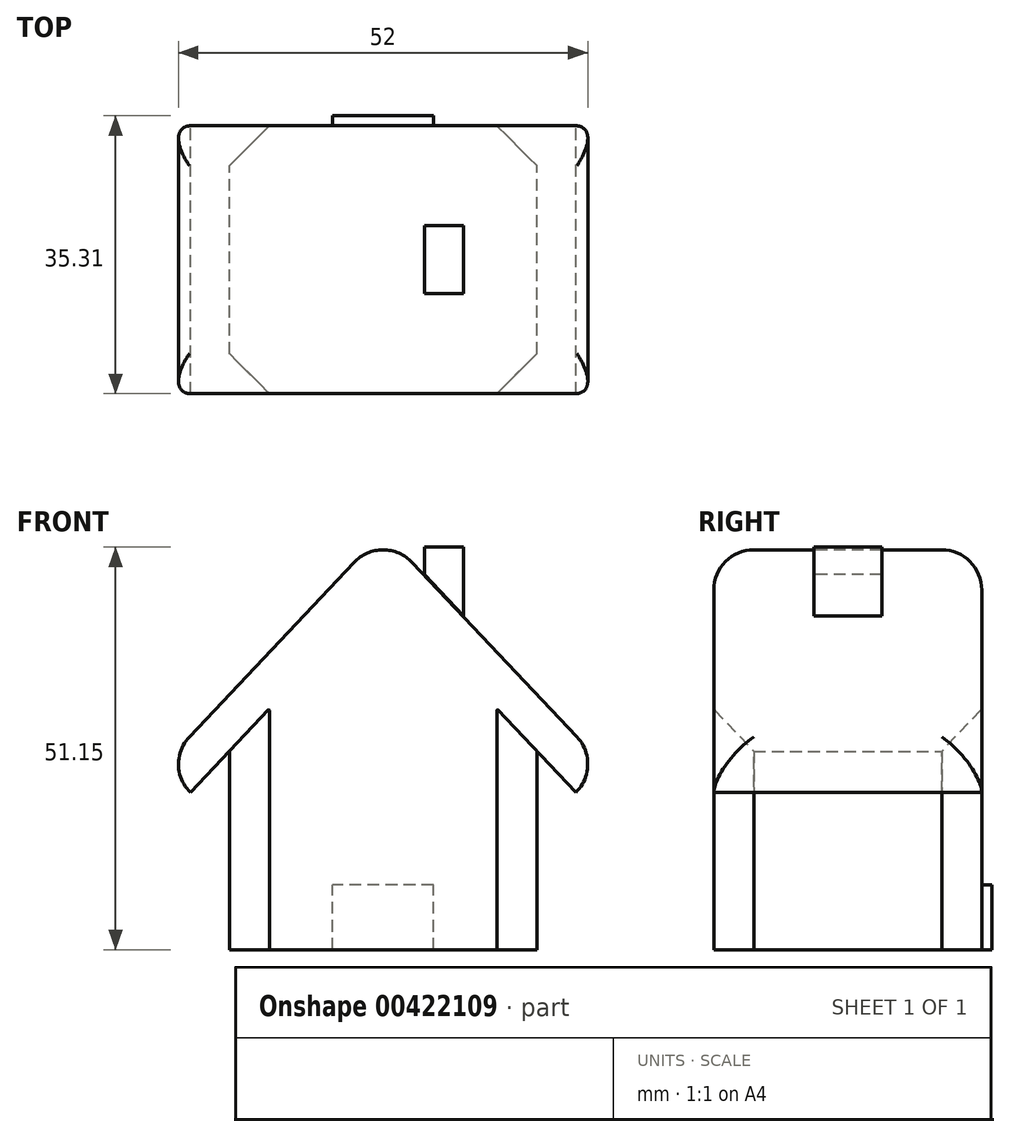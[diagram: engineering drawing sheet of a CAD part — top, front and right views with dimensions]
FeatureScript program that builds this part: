
annotation { "Feature Type Name" : "Feature", "Feature Type Description" : "" }
export const myFeature = defineFeature(function(context is Context, id is Id, definition is map)
    precondition{}
    {
        {
            var Q0;
            Q0=qCreatedBy(makeId("Front.planeOp"),FACE);
            var sketch = newSketch(context, id + "F0", { "sketchPlane" : qUnion([Q0])});
            skLineSegment(sketch, "E0", {"start": v(-19.53, 0) * mm, "end": v(-19.53, 25.21) * mm});
            skLineSegment(sketch, "E1", {"start": v(-19.53, 25.21) * mm, "end": v(-24.48, 19.97) * mm});
            skLineSegment(sketch, "E2", {"start": v(-24.48, 19.97) * mm, "end": v(-28.1, 23.38) * mm});
            skLineSegment(sketch, "E3", {"start": v(-28.1, 23.38) * mm, "end": v(0, 53.13) * mm});
            skLineSegment(sketch, "E4", {"start": v(-19.53, 0) * mm, "end": v(0, 0) * mm});
            skLineSegment(sketch, "E5.MirrorCS", {"start": v(28.1, 23.38) * mm, "end": v(0, 53.13) * mm});
            skLineSegment(sketch, "E6.MirrorCS", {"start": v(24.48, 19.97) * mm, "end": v(28.1, 23.38) * mm});
            skLineSegment(sketch, "E7.MirrorCS", {"start": v(19.53, 25.21) * mm, "end": v(24.48, 19.97) * mm});
            skLineSegment(sketch, "E8.MirrorCS", {"start": v(19.53, 0) * mm, "end": v(19.53, 25.21) * mm});
            skLineSegment(sketch, "E9.MirrorCS", {"start": v(19.53, 0) * mm, "end": v(0, 0) * mm});
            skSolve(sketch);
        }
        {
            var Q0;
            Q0=makeQuery(id+"F0.imprint","IMPRINT",FACE,{"disambiguationData":[TD([[makeQuery(id+"F0.imprint","IMPRINT",EDGE,{"derivedFrom":sQuery(id+"F0.wireOp",EDGE,"E0")}),-1.0]])]});
            extrude(context, id + "F1", {"entities" : qUnion([Q0]), "endBound" : BoundingType.SYMMETRIC, "depth" : 34.04 * mm});
        }
        {
            var Q0;
            Q0=makeQuery(id+"F1.opExtrude","CAP_FACE",FACE,{"disambiguationData":[OSD([sQuery(id+"F0.wireOp",EDGE,"E0"),sQuery(id+"F0.wireOp",EDGE,"E1"),sQuery(id+"F0.wireOp",EDGE,"E2"),sQuery(id+"F0.wireOp",EDGE,"E3"),sQuery(id+"F0.wireOp",EDGE,"E4"),sQuery(id+"F0.wireOp",EDGE,"E5.MirrorCS"),sQuery(id+"F0.wireOp",EDGE,"E6.MirrorCS"),sQuery(id+"F0.wireOp",EDGE,"E7.MirrorCS"),sQuery(id+"F0.wireOp",EDGE,"E8.MirrorCS"),sQuery(id+"F0.wireOp",EDGE,"E9.MirrorCS")])],"isStart":true});
            var sketch = newSketch(context, id + "F2", { "sketchPlane" : qUnion([Q0])});
            skLineSegment(sketch, "E10", {"start": v(-6.4, 0) * mm, "end": v(-6.4, 8.26) * mm});
            skLineSegment(sketch, "E11", {"start": v(0, 8.26) * mm, "end": v(-6.4, 8.26) * mm});
            skLineSegment(sketch, "E12", {"start": v(0, 8.26) * mm, "end": v(0, 0) * mm});
            skLineSegment(sketch, "E13", {"start": v(0, 0) * mm, "end": v(-6.4, 0) * mm});
            skLineSegment(sketch, "E14.MirrorCS", {"start": v(0, 8.26) * mm, "end": v(6.4, 8.26) * mm});
            skLineSegment(sketch, "E15.MirrorCS", {"start": v(6.4, 0) * mm, "end": v(6.4, 8.26) * mm});
            skLineSegment(sketch, "E16.MirrorCS", {"start": v(0, 0) * mm, "end": v(6.4, 0) * mm});
            skSolve(sketch);
        }
        {
            var Q0;
            Q0=makeQuery(id+"F2.imprint","IMPRINT",FACE,{"disambiguationData":[TD([[makeQuery(id+"F2.imprint","IMPRINT",EDGE,{"derivedFrom":sQuery(id+"F2.wireOp",EDGE,"E12")}),1.0]])]});
            var Q1;
            Q1=makeQuery(id+"F2.imprint","IMPRINT",FACE,{"disambiguationData":[TD([[makeQuery(id+"F2.imprint","IMPRINT",EDGE,{"derivedFrom":sQuery(id+"F2.wireOp",EDGE,"E10")}),-1.0]])]});
            extrude(context, id + "F3", {"entities" : qUnion([Q0, Q1]), "operationType" : NewBodyOperationType.ADD, "depth" : 1.27 * mm});
        }
        {
            var Q0;
            Q0=qCreatedBy(makeId("Front.planeOp"),FACE);
            var sketch = newSketch(context, id + "F4", { "sketchPlane" : qUnion([Q0])});
            skLineSegment(sketch, "E17", {"start": v(10.2, 42.4) * mm, "end": v(10.2, 51.15) * mm});
            skLineSegment(sketch, "E18", {"start": v(10.2, 51.15) * mm, "end": v(5.25, 51.15) * mm});
            skLineSegment(sketch, "E19", {"start": v(5.25, 47.66) * mm, "end": v(5.25, 51.15) * mm});
            skLineSegment(sketch, "E20", {"start": v(10.2, 42.4) * mm, "end": v(5.25, 47.66) * mm});
            skSolve(sketch);
        }
        {
            var Q0;
            Q0 = qSketchRegion(id + "F4", true);
            extrude(context, id + "F5", {"entities" : qUnion([Q0]), "endBound" : BoundingType.SYMMETRIC, "oppositeDirection" : true, "depth" : 8.64 * mm});
        }
        {
            var Q0;
            Q0=makeQuery(id+"F1.opExtrude","SWEPT_FACE",FACE,{"disambiguationData":[OSD([sQuery(id+"F0.wireOp",EDGE,"E5.MirrorCS")])]});
            var Q1;
            Q1=makeQuery(id+"F1.opExtrude","SWEPT_FACE",FACE,{"disambiguationData":[OSD([sQuery(id+"F0.wireOp",EDGE,"E3")])]});
            fillet(context, id + "F6", {"entities" : qUnion([Q0, Q1]), "radius" : 5.08 * mm, "tangentPropagation" : true, "allowEdgeOverflow" : false});
        }
        {
            var Q0;
            Q0=makeQuery(id+"F1.opExtrude","CAP_EDGE",EDGE,{"disambiguationData":[OSD([sQuery(id+"F0.wireOp",EDGE,"E8.MirrorCS")])],"isStart":true});
            var Q1;
            Q1=makeQuery(id+"F1.opExtrude","CAP_EDGE",EDGE,{"disambiguationData":[OSD([sQuery(id+"F0.wireOp",EDGE,"E0")])],"isStart":true});
            var Q2;
            Q2=makeQuery(id+"F1.opExtrude","CAP_EDGE",EDGE,{"disambiguationData":[OSD([sQuery(id+"F0.wireOp",EDGE,"E8.MirrorCS")])],"isStart":false});
            var Q3;
            Q3=makeQuery(id+"F1.opExtrude","CAP_EDGE",EDGE,{"disambiguationData":[OSD([sQuery(id+"F0.wireOp",EDGE,"E0")])],"isStart":false});
            chamfer(context, id + "F7", {"entities" : qUnion([Q0, Q1, Q2, Q3]), "width" : 5.08 * mm, "tangentPropagation" : true});
        }
    });
